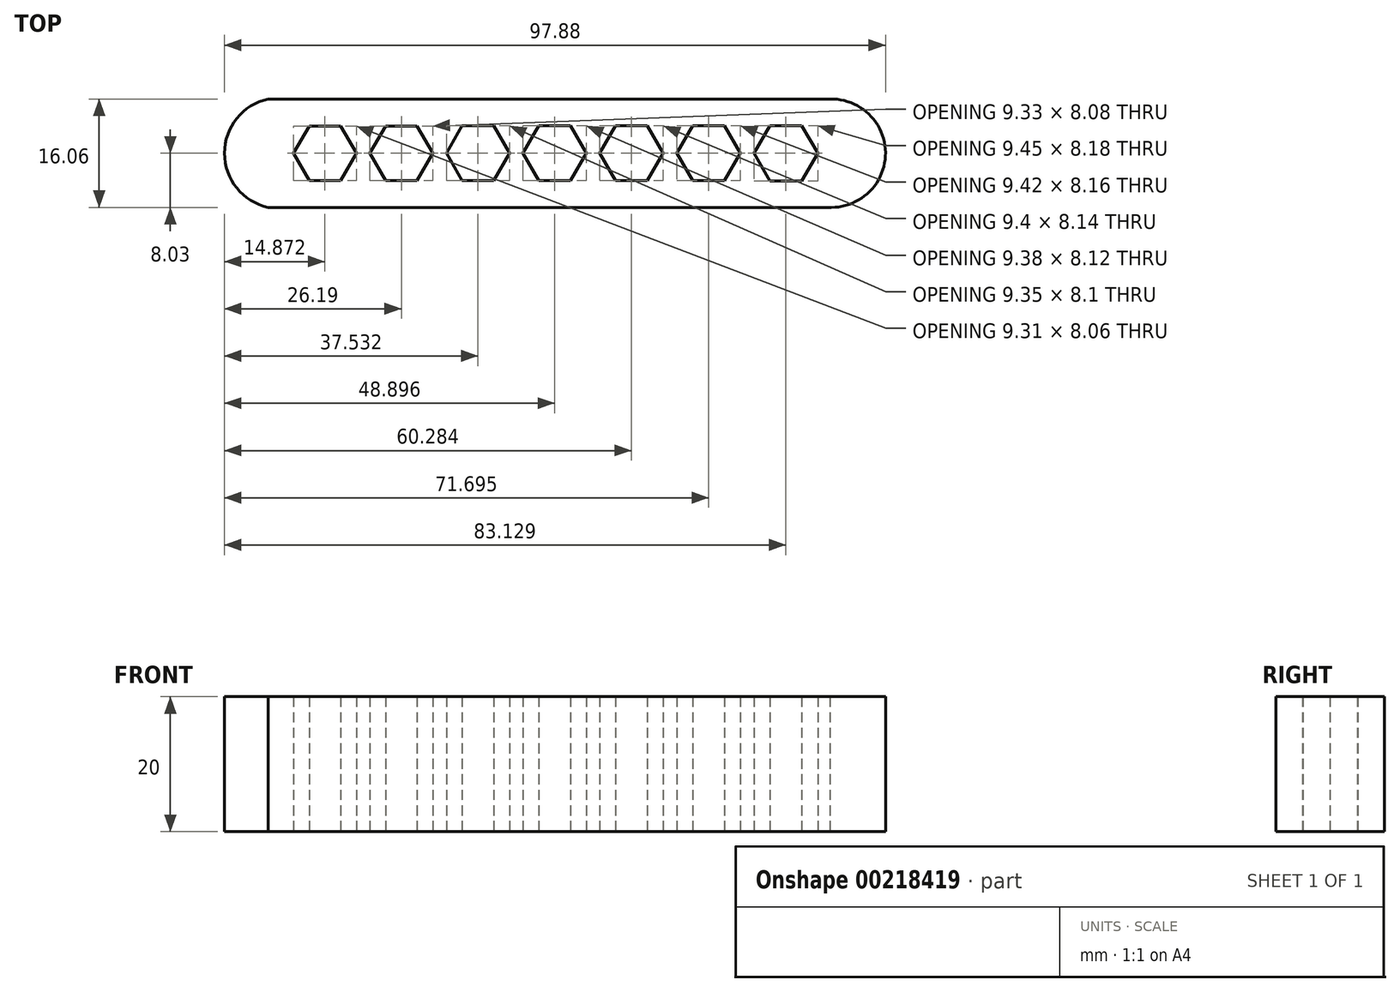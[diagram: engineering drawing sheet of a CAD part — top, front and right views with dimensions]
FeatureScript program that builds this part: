
annotation { "Feature Type Name" : "Feature", "Feature Type Description" : "" }
export const myFeature = defineFeature(function(context is Context, id is Id, definition is map)
    precondition{}
    {
        {
            var Q0;
            Q0=qCreatedBy(makeId("Top.planeOp"),FACE);
            var sketch = newSketch(context, id + "F0", { "sketchPlane" : qUnion([Q0])});
            skCircle(sketch, "E0.cCircle", {"center": v(-31.24, 0) * mm, "radius": 4.03 * mm, "construction": true});
            skLineSegment(sketch, "E0.0", {"start": v(-28.91, -4.03) * mm, "end": v(-33.56, -4.03) * mm});
            skLineSegment(sketch, "E0.1", {"start": v(-33.56, -4.03) * mm, "end": v(-35.9, 0) * mm});
            skLineSegment(sketch, "E0.2", {"start": v(-35.9, 0) * mm, "end": v(-33.56, 4.03) * mm});
            skLineSegment(sketch, "E0.3", {"start": v(-33.56, 4.03) * mm, "end": v(-28.91, 4.03) * mm});
            skLineSegment(sketch, "E0.4", {"start": v(-28.91, 4.03) * mm, "end": v(-26.58, 0) * mm});
            skLineSegment(sketch, "E0.5", {"start": v(-26.58, 0) * mm, "end": v(-28.91, -4.03) * mm});
            skPoint(sketch, "E0.0.midPoint", {"position": v(-31.24, -4.03) * mm});
            skCircle(sketch, "E1.cCircle", {"center": v(-8.58, 0) * mm, "radius": 4.05 * mm, "construction": true});
            skLineSegment(sketch, "E1.0", {"start": v(-10.92, 4.05) * mm, "end": v(-6.24, 4.05) * mm});
            skLineSegment(sketch, "E1.1", {"start": v(-6.24, 4.05) * mm, "end": v(-3.9, 0) * mm});
            skLineSegment(sketch, "E1.2", {"start": v(-3.9, 0) * mm, "end": v(-6.24, -4.05) * mm});
            skLineSegment(sketch, "E1.3", {"start": v(-6.24, -4.05) * mm, "end": v(-10.92, -4.05) * mm});
            skLineSegment(sketch, "E1.4", {"start": v(-10.92, -4.05) * mm, "end": v(-13.25, 0) * mm});
            skLineSegment(sketch, "E1.5", {"start": v(-13.25, 0) * mm, "end": v(-10.92, 4.05) * mm});
            skPoint(sketch, "E1.0.midPoint", {"position": v(-8.58, 4.05) * mm});
            skCircle(sketch, "E2.cCircle", {"center": v(2.79, 0) * mm, "radius": 4.06 * mm, "construction": true});
            skLineSegment(sketch, "E2.0", {"start": v(0.44, 4.06) * mm, "end": v(5.13, 4.06) * mm});
            skLineSegment(sketch, "E2.1", {"start": v(5.13, 4.06) * mm, "end": v(7.47, 0) * mm});
            skLineSegment(sketch, "E2.2", {"start": v(7.47, 0) * mm, "end": v(5.13, -4.06) * mm});
            skLineSegment(sketch, "E2.3", {"start": v(5.13, -4.06) * mm, "end": v(0.44, -4.06) * mm});
            skLineSegment(sketch, "E2.4", {"start": v(0.44, -4.06) * mm, "end": v(-1.9, 0) * mm});
            skLineSegment(sketch, "E2.5", {"start": v(-1.9, 0) * mm, "end": v(0.44, 4.06) * mm});
            skPoint(sketch, "E2.0.midPoint", {"position": v(2.79, 4.06) * mm});
            skCircle(sketch, "E3.cCircle", {"center": v(14.17, 0) * mm, "radius": 4.07 * mm, "construction": true});
            skLineSegment(sketch, "E3.0", {"start": v(11.82, 4.07) * mm, "end": v(16.52, 4.07) * mm});
            skLineSegment(sketch, "E3.1", {"start": v(16.52, 4.07) * mm, "end": v(18.87, 0) * mm});
            skLineSegment(sketch, "E3.2", {"start": v(18.87, 0) * mm, "end": v(16.52, -4.07) * mm});
            skLineSegment(sketch, "E3.3", {"start": v(16.52, -4.07) * mm, "end": v(11.82, -4.07) * mm});
            skLineSegment(sketch, "E3.4", {"start": v(11.82, -4.07) * mm, "end": v(9.47, 0) * mm});
            skLineSegment(sketch, "E3.5", {"start": v(9.47, 0) * mm, "end": v(11.82, 4.07) * mm});
            skPoint(sketch, "E3.0.midPoint", {"position": v(14.17, 4.07) * mm});
            skCircle(sketch, "E4.cCircle", {"center": v(25.58, 0) * mm, "radius": 4.08 * mm, "construction": true});
            skLineSegment(sketch, "E4.0", {"start": v(23.23, 4.08) * mm, "end": v(27.94, 4.08) * mm});
            skLineSegment(sketch, "E4.1", {"start": v(27.94, 4.08) * mm, "end": v(30.3, 0) * mm});
            skLineSegment(sketch, "E4.2", {"start": v(30.3, 0) * mm, "end": v(27.94, -4.08) * mm});
            skLineSegment(sketch, "E4.3", {"start": v(27.94, -4.08) * mm, "end": v(23.23, -4.08) * mm});
            skLineSegment(sketch, "E4.4", {"start": v(23.23, -4.08) * mm, "end": v(20.87, 0) * mm});
            skLineSegment(sketch, "E4.5", {"start": v(20.87, 0) * mm, "end": v(23.23, 4.08) * mm});
            skPoint(sketch, "E4.0.midPoint", {"position": v(25.58, 4.08) * mm});
            skCircle(sketch, "E5.cCircle", {"center": v(37.02, 0) * mm, "radius": 4.1 * mm, "construction": true});
            skLineSegment(sketch, "E5.0", {"start": v(34.66, 4.1) * mm, "end": v(39.38, 4.1) * mm});
            skLineSegment(sketch, "E5.1", {"start": v(39.38, 4.1) * mm, "end": v(41.74, 0) * mm});
            skLineSegment(sketch, "E5.2", {"start": v(41.74, 0) * mm, "end": v(39.38, -4.1) * mm});
            skLineSegment(sketch, "E5.3", {"start": v(39.38, -4.1) * mm, "end": v(34.66, -4.1) * mm});
            skLineSegment(sketch, "E5.4", {"start": v(34.66, -4.1) * mm, "end": v(32.3, 0) * mm});
            skLineSegment(sketch, "E5.5", {"start": v(32.3, 0) * mm, "end": v(34.66, 4.1) * mm});
            skPoint(sketch, "E5.0.midPoint", {"position": v(37.02, 4.1) * mm});
            skLineSegment(sketch, "E6", {"start": v(-39.62, 8.03) * mm, "end": v(43.54, 8.03) * mm});
            skLineSegment(sketch, "E7", {"start": v(43.74, -8.03) * mm, "end": v(-39.62, -8.03) * mm});
            skArc(sketch, "E8", {"start": v(-39.62, 8.03) * mm, "mid": v(-46.1, 0) * mm, "end": v(-39.62, -8.03) * mm});
            skArc(sketch, "E9", {"start": v(43.74, -8.03) * mm, "mid": v(51.77, 0.1) * mm, "end": v(43.54, 8.03) * mm});
            skCircle(sketch, "E10.cCircle", {"center": v(-19.92, 0) * mm, "radius": 4.04 * mm, "construction": true});
            skLineSegment(sketch, "E10.0", {"start": v(-17.59, 4.04) * mm, "end": v(-15.25, 0) * mm});
            skLineSegment(sketch, "E10.1", {"start": v(-15.25, 0) * mm, "end": v(-17.59, -4.04) * mm});
            skLineSegment(sketch, "E10.2", {"start": v(-17.59, -4.04) * mm, "end": v(-22.25, -4.04) * mm});
            skLineSegment(sketch, "E10.3", {"start": v(-22.25, -4.04) * mm, "end": v(-24.58, 0) * mm});
            skLineSegment(sketch, "E10.4", {"start": v(-24.58, 0) * mm, "end": v(-22.25, 4.04) * mm});
            skLineSegment(sketch, "E10.5", {"start": v(-22.25, 4.04) * mm, "end": v(-17.59, 4.04) * mm});
            skPoint(sketch, "E10.0.midPoint", {"position": v(-16.42, 2.02) * mm});
            skSolve(sketch);
        }
        {
            var Q0;
            Q0=makeQuery(id+"F0.imprint","IMPRINT",FACE,{"disambiguationData":[TD([[makeQuery(id+"F0.imprint","IMPRINT",EDGE,{"derivedFrom":sQuery(id+"F0.wireOp",EDGE,"E0.0")}),1.0]])]});
            extrude(context, id + "F1", {"entities" : qUnion([Q0]), "depth" : 20 * mm});
        }
    });
